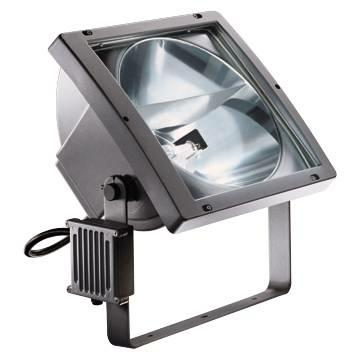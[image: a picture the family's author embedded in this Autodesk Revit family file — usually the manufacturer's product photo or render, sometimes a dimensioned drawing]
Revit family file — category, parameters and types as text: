
# Revit family: Lighting-Floodlights-GEWISS-COLOSSEUM_OTTICA_CIRCULAR
name_source: partatom
category: Apparecchi per illuminazione
units: mm (PartAtom-declared; Revit-internal decimal feet)

## family parameters
Condiviso = No
Host = Superficie
Numero OmniClass = 23.80.70.11.14
Punto di calcolo locali = Sì
Quota connettore circolare = Usa diametro
Sorgente d'illuminazione = No
Taglio con vuoti quando caricato = No
Tipo di parte = Normale
Titolo OmniClass = General Luminaries, Directional

## types (6) — shared parameters
Application = External
Carico apparente = 2000 VA
Catalogue = LIGHTING
Catalogue Range = COLOSSEUM
Classificazione carico = Illuminazione
Colour = Graphite grey
DIN 18032-3 certification = Complying
Electrocod = 2433
IDF = 0415cf78-a531-4e92-83dd-7aec1197f31b
IDT = 36e0c751-5da2-4f5b-b782-3005ce20383a
IP degree = IP66
Immagine tipo = GW84656.jpg
Insulation class = I
L_interna staffa = 515 mm  [stored 1.68963 ft]
Lamp = MN
Lamp holder = K12s/Cable
Lampada = MN
Lateral surface exposed to the wind = 0,083M2
Light pollution = 0 cd/Klm
Manopola di rotazione = <Per categoria>
Material = Aluminium
Maximum surface exposed to the wind = 0,25M2
Minimum distance from the illuminated object = 3M
Numero di poli = 2
Optic = Circular - ULOR: 0%
Produttore = GEWISS S.p.A.
Prospetto di default = 1219 mm
SEO = Floodlight
Shock resistance = IK09
Spessore staffa = 40 mm  [stored 0.131234 ft]
Staffa = <Per categoria>
Technical sheet = https://www.gewiss.com
URL = https://www.gewiss.com
Version file RFA = 20.11
Voltaggio = 230 V
Weight (kg) = 16
Weight (kg): = 16

## per-type parameters (varying)
| type | Beam | Descrizione | EAN code | Lamp current | Lamp current: | Lamp power | Modello |
| GW84756 - COLOSSEUM CIR. BEAM DIFF. 1000W MN | Diffused - 20° | COLOSSEUM CIR. BEAM DIFF. 1000W MN | 8011564100015 | 9,6 | 9,6A | 1000W | GW84756 |
| GW84656 - COLOSSEUM CIR. BEAM RES. 1000W MN | Restricted - 8° | COLOSSEUM CIR. BEAM RES. 1000W MN | 8011564065734 | 9,6 | 9,6A | 1000W | GW84656 |
| GW84754 - COLOSSEUM CIR. BEAM MEDIUM 1000W MN | Medium - 10° | COLOSSEUM CIR. BEAM MEDIUM 1000W MN | 8011564099999 | 9,6 | 9,6A | 1000W | GW84754 |
| GW84657 - COLOSSEUM CIR. BEAM RES. 2000W MN | Restricted - 8° | COLOSSEUM CIR. BEAM RES. 2000W MN | 8011564065765 | 11,3A | 11,3A | 2000W | GW84657 |
| GW84755 - COLOSSEUM CIR. BEAM MEDIUM 2000W MN | Medium - 10° | COLOSSEUM CIR. BEAM MEDIUM 2000W MN | 8011564100008 | 11,3A | 11,3A | 2000W | GW84755 |
| GW84757 - COLOSSEUM CIR. BEAM DIFF. 2000W MN | Diffused - 20° | COLOSSEUM CIR. BEAM DIFF. 2000W MN | 8011564100022 | 11,3A | 11,3A | 2000W | GW84757 |

note: [stored X ft] marks values corroborated as IEEE doubles in the binary element streams (Revit-internal decimal feet)
